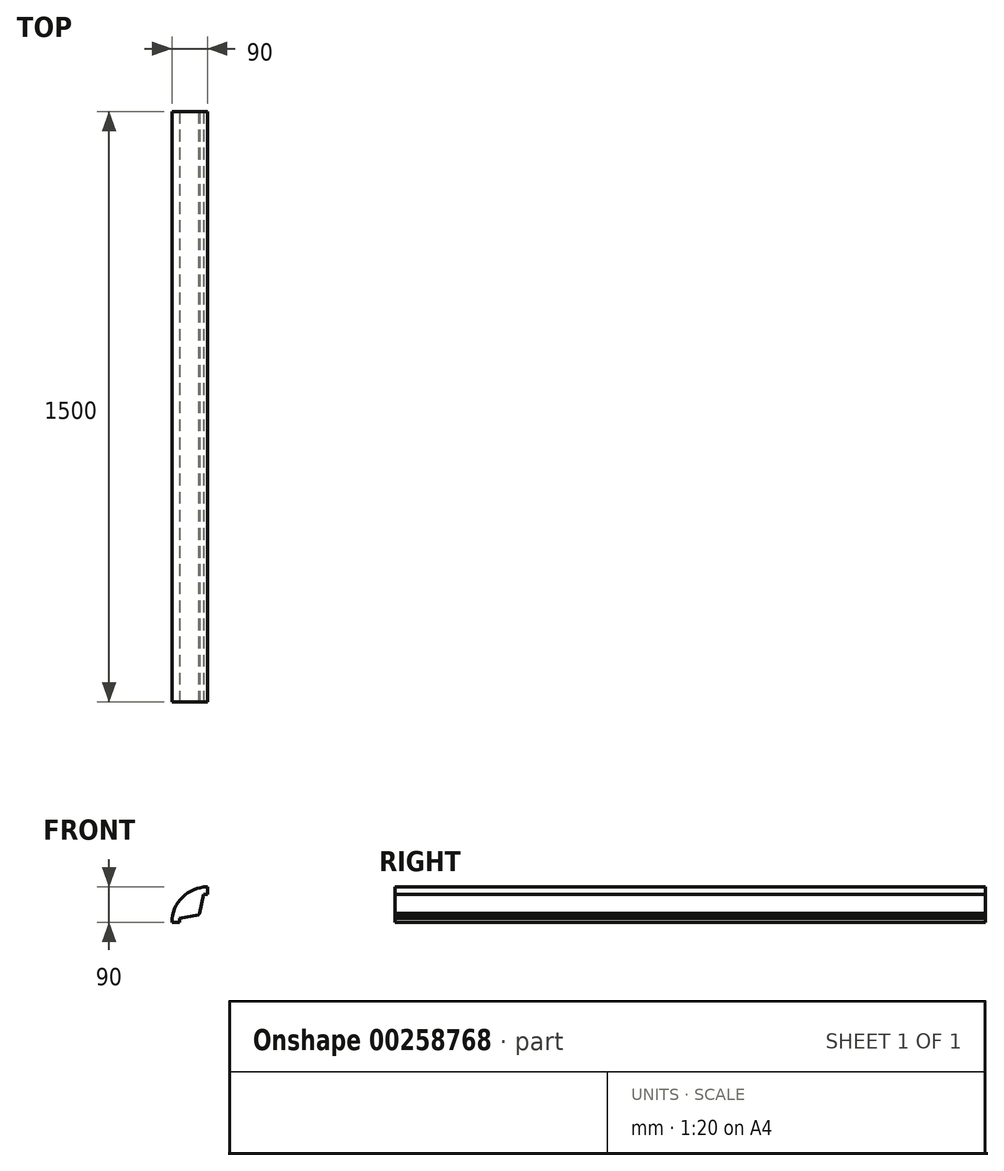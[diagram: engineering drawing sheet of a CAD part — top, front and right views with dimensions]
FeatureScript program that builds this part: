
annotation { "Feature Type Name" : "Feature", "Feature Type Description" : "" }
export const myFeature = defineFeature(function(context is Context, id is Id, definition is map)
    precondition{}
    {
        {
            var Q0;
            Q0=qCreatedBy(makeId("Front.planeOp"),FACE);
            var sketch = newSketch(context, id + "F0", { "sketchPlane" : qUnion([Q0])});
            skArc(sketch, "E0", {"start": v(0, 90) * mm, "mid": v(-63.64, 63.64) * mm, "end": v(-90, 0) * mm});
            skArc(sketch, "E1", {"start": v(-19.48, 22.81) * mm, "mid": v(-21.21, 21.21) * mm, "end": v(-22.81, 19.48) * mm});
            skLineSegment(sketch, "E2", {"start": v(-70.89, 10) * mm, "end": v(-70.89, 0) * mm});
            skLineSegment(sketch, "E3", {"start": v(-70.89, 10) * mm, "end": v(-22.81, 19.48) * mm});
            skLineSegment(sketch, "E4.3.3.0", {"start": v(0, 70.89) * mm, "end": v(-10, 70.89) * mm});
            skLineSegment(sketch, "E4.6.3.0", {"start": v(-10, 70.89) * mm, "end": v(-19.48, 22.81) * mm});
            skPoint(sketch, "E5.endSnap0", {"position": v(-70.89, 0) * mm});
            skLineSegment(sketch, "E6", {"start": v(0, 70.89) * mm, "end": v(0, 90) * mm});
            skPoint(sketch, "E6.endSnap0", {"position": v(0, 70.89) * mm});
            skLineSegment(sketch, "E7.trimOffspring", {"start": v(-70.89, 0) * mm, "end": v(-90, 0) * mm});
            skSolve(sketch);
        }
        {
            var Q0;
            Q0=makeQuery(id+"F0.imprint","IMPRINT",FACE,{"disambiguationData":[TD([[makeQuery(id+"F0.imprint","IMPRINT",EDGE,{"derivedFrom":sQuery(id+"F0.wireOp",EDGE,"E0")}),1.0]])]});
            extrude(context, id + "F1", {"entities" : qUnion([Q0]), "oppositeDirection" : true, "depth" : 1500 * mm});
        }
    });
